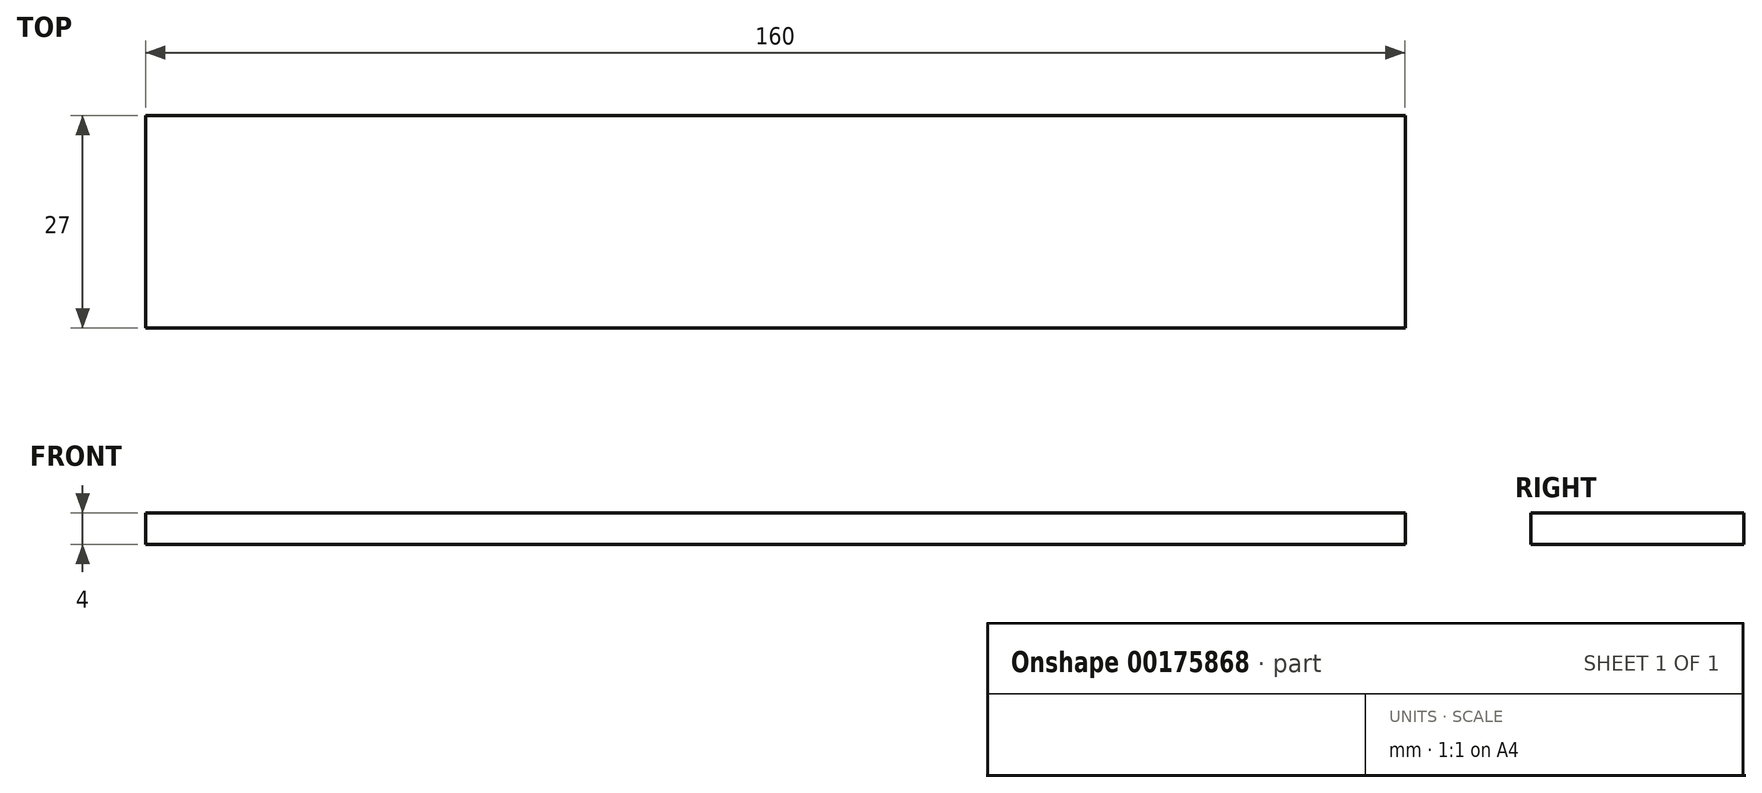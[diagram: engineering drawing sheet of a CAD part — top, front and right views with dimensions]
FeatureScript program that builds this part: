
annotation { "Feature Type Name" : "Feature", "Feature Type Description" : "" }
export const myFeature = defineFeature(function(context is Context, id is Id, definition is map)
    precondition{}
    {
        {
            var Q0;
            Q0=qCreatedBy(makeId("Top.planeOp"),FACE);
            var sketch = newSketch(context, id + "F0", { "sketchPlane" : qUnion([Q0])});
            skLineSegment(sketch, "E0.bottom", {"start": v(-120.49, -8.6) * mm, "end": v(39.51, -8.6) * mm});
            skLineSegment(sketch, "E0.top", {"start": v(-120.49, -35.6) * mm, "end": v(39.51, -35.6) * mm});
            skLineSegment(sketch, "E0.left", {"start": v(-120.49, -8.6) * mm, "end": v(-120.49, -35.6) * mm});
            skLineSegment(sketch, "E0.right", {"start": v(39.51, -8.6) * mm, "end": v(39.51, -35.6) * mm});
            skSolve(sketch);
        }
        {
            var Q0;
            Q0=qSketchRegion(id+"F0",true);
            extrude(context, id + "F1", {"entities" : qUnion([Q0]), "depth" : 4 * mm});
        }
    });
